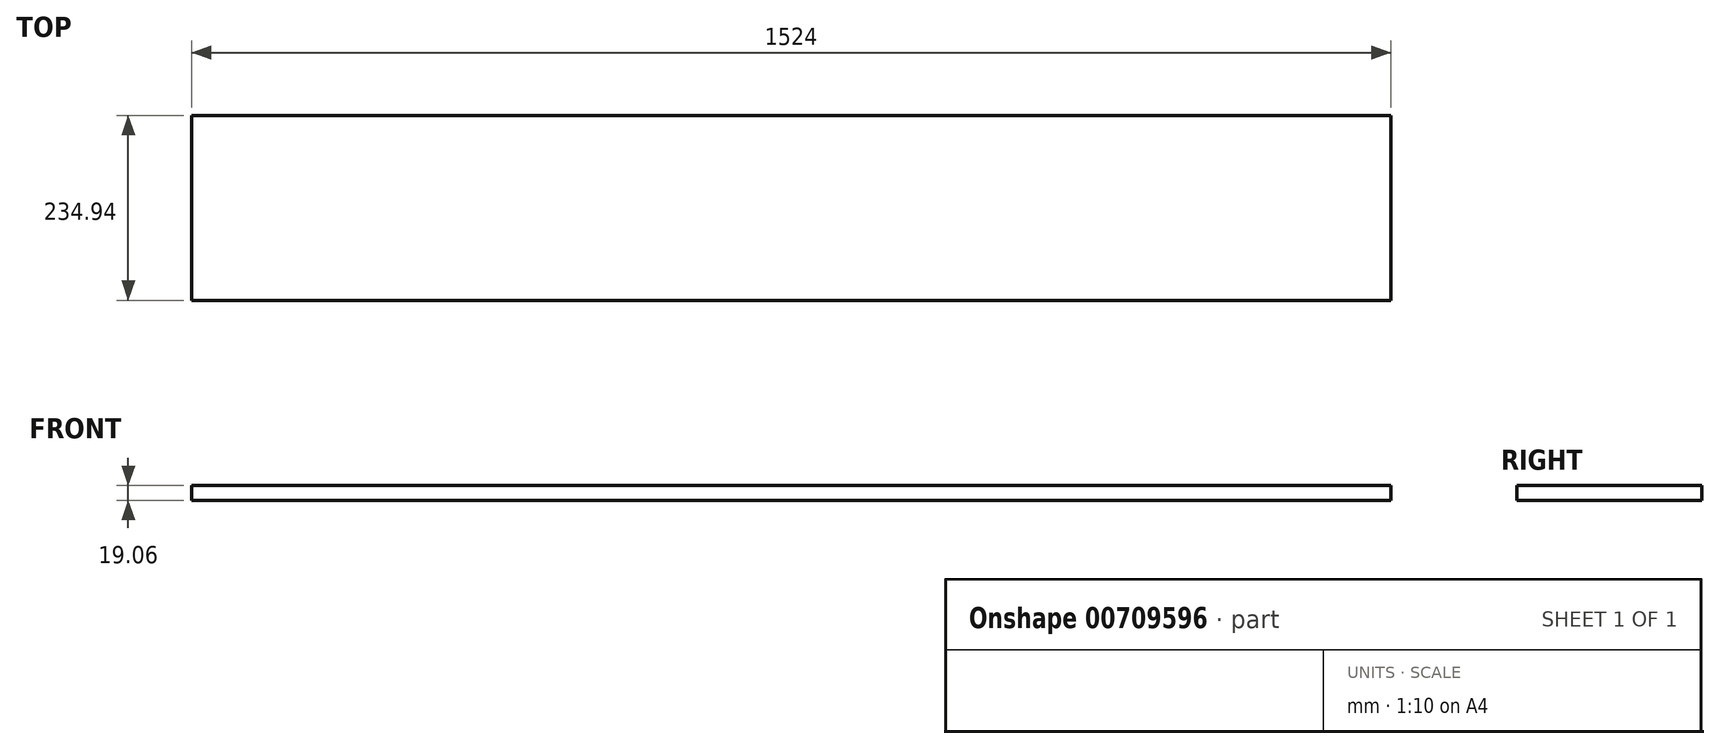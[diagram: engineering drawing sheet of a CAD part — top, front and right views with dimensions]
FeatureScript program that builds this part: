
annotation { "Feature Type Name" : "Feature", "Feature Type Description" : "" }
export const myFeature = defineFeature(function(context is Context, id is Id, definition is map)
    precondition{}
    {
        {
            var Q0;
            Q0=qCreatedBy(makeId("Top.planeOp"),FACE);
            var sketch = newSketch(context, id + "F0", { "sketchPlane" : qUnion([Q0])});
            skLineSegment(sketch, "E0.bottom", {"start": v(762, -117.47) * mm, "end": v(-762, -117.48) * mm});
            skLineSegment(sketch, "E0.top", {"start": v(762, 117.48) * mm, "end": v(-762, 117.47) * mm});
            skLineSegment(sketch, "E0.left", {"start": v(762, -117.47) * mm, "end": v(762, 117.48) * mm});
            skLineSegment(sketch, "E0.right", {"start": v(-762, -117.48) * mm, "end": v(-762, 117.47) * mm});
            skPoint(sketch, "E0.middle", {"position": v(0, 0) * mm});
            skSolve(sketch);
        }
        {
            var Q0;
            Q0=makeQuery(id+"F0.imprint","IMPRINT",FACE,{"disambiguationData":[TD([[makeQuery(id+"F0.imprint","IMPRINT",EDGE,{"derivedFrom":sQuery(id+"F0.wireOp",EDGE,"E0.bottom")}),-1.0]])]});
            extrude(context, id + "F1", {"entities" : qUnion([Q0]), "endBound" : BoundingType.SYMMETRIC, "depth" : 19.05 * mm, "offsetDistance" : 25.4 * mm});
        }
    });
